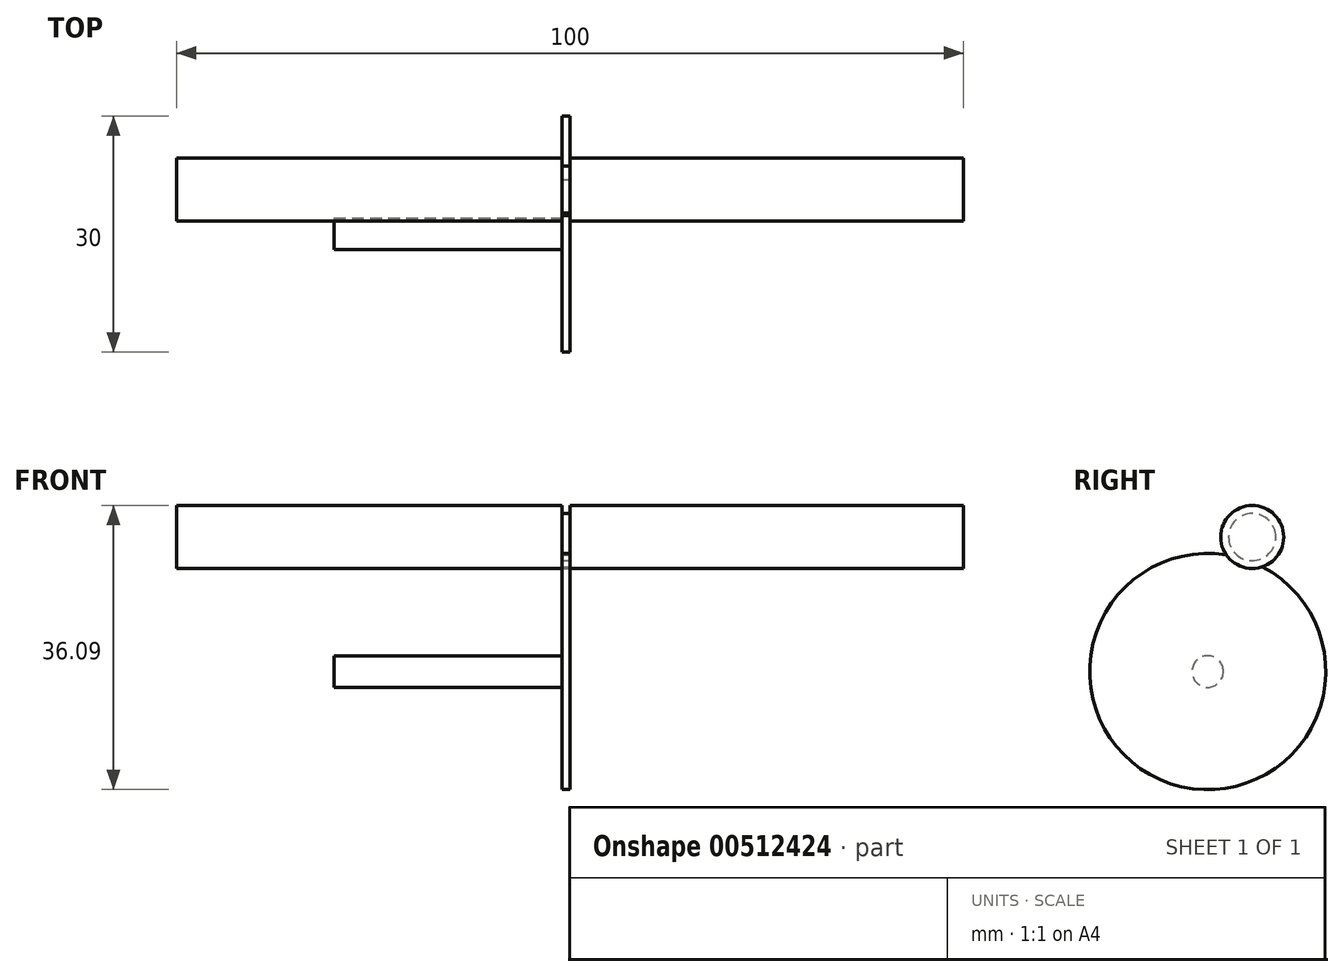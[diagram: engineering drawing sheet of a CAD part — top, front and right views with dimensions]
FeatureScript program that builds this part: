
annotation { "Feature Type Name" : "Feature", "Feature Type Description" : "" }
export const myFeature = defineFeature(function(context is Context, id is Id, definition is map)
    precondition{}
    {
        {
            var Q0;
            Q0=qCreatedBy(makeId("Right.planeOp"),FACE);
            var sketch = newSketch(context, id + "F0", { "sketchPlane" : qUnion([Q0])});
            skCircle(sketch, "E0", {"center": v(0, 0) * mm, "radius": 4 * mm});
            skCircle(sketch, "E1", {"center": v(0, 0) * mm, "radius": 3 * mm});
            skCircle(sketch, "E2", {"center": v(-5.65, -17.09) * mm, "radius": 15 * mm});
            skCircle(sketch, "E3", {"center": v(-5.65, -17.09) * mm, "radius": 2 * mm});
            skSolve(sketch);
        }
        {
            var Q0;
            Q0=makeQuery(id+"F0.imprint","IMPRINT",FACE,{"disambiguationData":[TD([[makeQuery(id+"F0.imprint","IMPRINT",EDGE,{"derivedFrom":sQuery(id+"F0.wireOp",EDGE,"E0")}),1.0]])]});
            var Q1;
            Q1=makeQuery(id+"F0.imprint","IMPRINT",FACE,{"disambiguationData":[TD([[makeQuery(id+"F0.imprint","IMPRINT",EDGE,{"derivedFrom":sQuery(id+"F0.wireOp",EDGE,"E1")}),1.0]])]});
            var Q2;
            {var subQ4=sQuery(id+"F0.wireOp",EDGE,"E1");Q2=makeQuery(id+"F0.imprint","IMPRINT",FACE,{"disambiguationData":[TD([[makeQuery(id+"F0.imprint","IMPRINT",EDGE,{"derivedFrom":subQ4}),-1.0]])]});}
            extrude(context, id + "F1", {"entities" : qUnion([Q0, Q1, Q2]), "depth" : 50 * mm, "hasSecondDirection" : true, "secondDirectionOppositeDirection" : true, "secondDirectionDepth" : 50 * mm});
        }
        {
            var Q0;
            {var subQ4=sQuery(id+"F0.wireOp",EDGE,"E1");Q0=makeQuery(id+"F0.imprint","IMPRINT",FACE,{"disambiguationData":[TD([[makeQuery(id+"F0.imprint","IMPRINT",EDGE,{"derivedFrom":subQ4}),-1.0]])]});}
            var Q1;
            {var subQ0=sQuery(id+"F0.wireOp",EDGE,"E2");var subQ1=sQuery(id+"F0.wireOp",EDGE,"E0");var subQ2=makeQuery(id+"F0.imprint","INTERSECT",VERTEX,{"disambiguationData":[OD(0.0)],"derivedFrom":[subQ1,subQ0]});Q1=makeQuery(id+"F0.imprint","IMPRINT",FACE,{"disambiguationData":[TD([[makeQuery(id+"F0.imprint","IMPRINT",EDGE,{"disambiguationData":[TD([[subQ2,1.0]])],"derivedFrom":subQ1}),1.0]])]});}
            extrude(context, id + "F2", {"entities" : qUnion([Q0, Q1]), "operationType" : NewBodyOperationType.REMOVE, "oppositeDirection" : true, "depth" : 1 * mm});
        }
        {
            var Q0;
            Q0=makeQuery(id+"F0.imprint","IMPRINT",FACE,{"disambiguationData":[TD([[makeQuery(id+"F0.imprint","IMPRINT",EDGE,{"derivedFrom":sQuery(id+"F0.wireOp",EDGE,"E3")}),-1.0]])]});
            extrude(context, id + "F3", {"entities" : qUnion([Q0]), "oppositeDirection" : true, "depth" : 1 * mm});
        }
        {
            var Q0;
            Q0=makeQuery(id+"F0.imprint","IMPRINT",FACE,{"disambiguationData":[TD([[makeQuery(id+"F0.imprint","IMPRINT",EDGE,{"derivedFrom":sQuery(id+"F0.wireOp",EDGE,"E3")}),1.0]])]});
            extrude(context, id + "F4", {"entities" : qUnion([Q0]), "operationType" : NewBodyOperationType.ADD, "oppositeDirection" : true, "depth" : 30 * mm});
        }
    });
